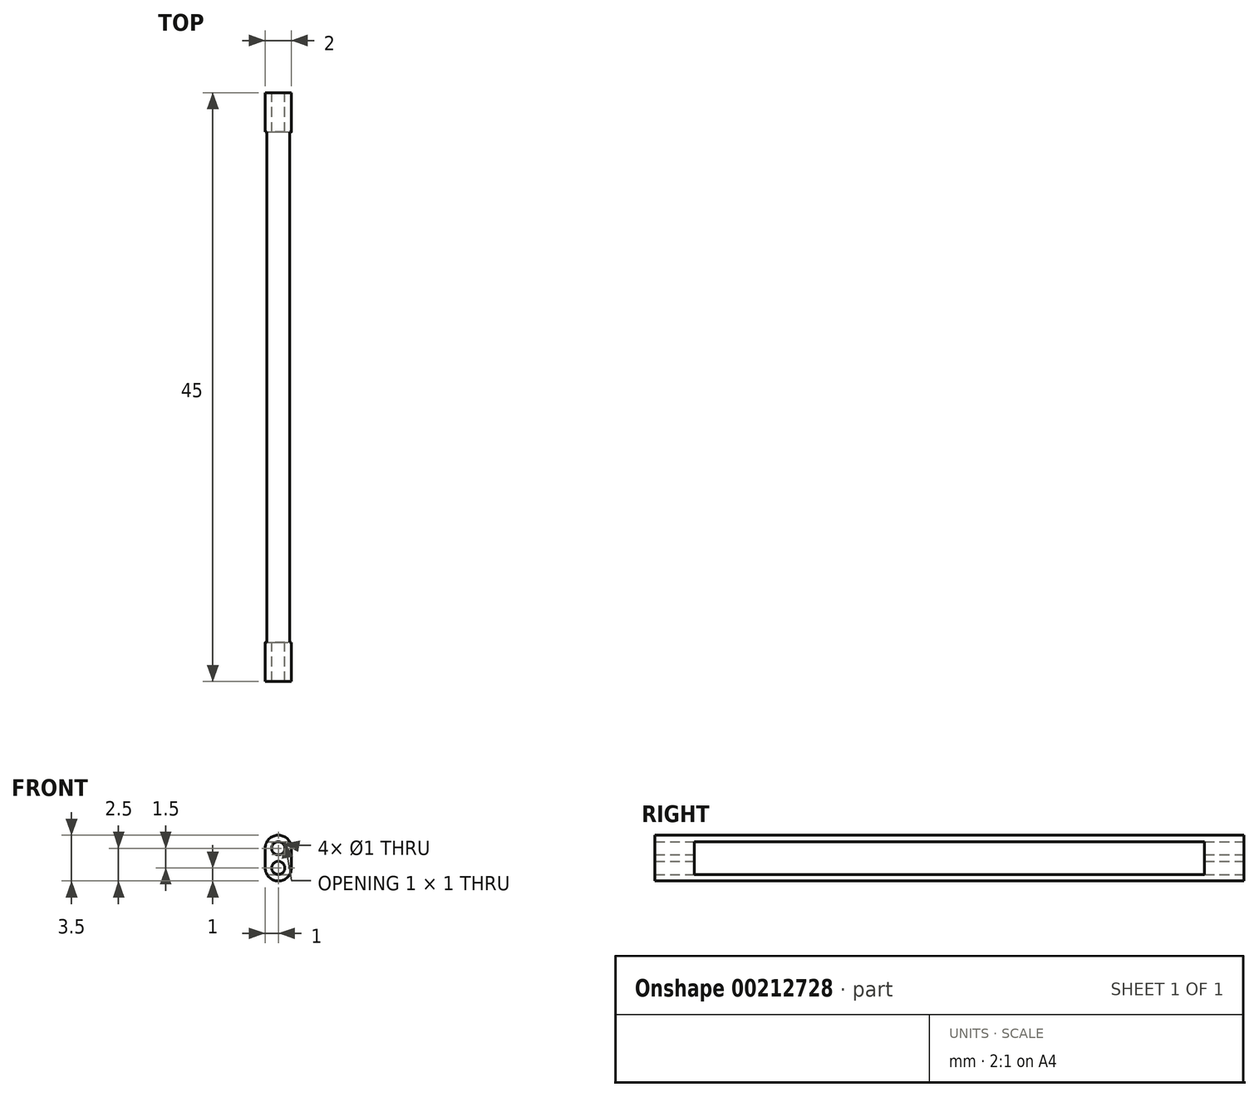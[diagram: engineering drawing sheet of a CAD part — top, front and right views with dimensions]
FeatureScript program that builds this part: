
annotation { "Feature Type Name" : "Feature", "Feature Type Description" : "" }
export const myFeature = defineFeature(function(context is Context, id is Id, definition is map)
    precondition{}
    {
        {
            var Q0;
            Q0=qCreatedBy(makeId("Front.planeOp"),FACE);
            var sketch = newSketch(context, id + "F0", { "sketchPlane" : qUnion([Q0])});
            skLineSegment(sketch, "E0.left", {"start": v(1, -0.75) * mm, "end": v(1, 0.75) * mm});
            skLineSegment(sketch, "E0.right", {"start": v(-1, -0.75) * mm, "end": v(-1, 0.75) * mm});
            skPoint(sketch, "E0.middle", {"position": v(0, 0) * mm});
            skCircle(sketch, "E1", {"center": v(0, 0.75) * mm, "radius": 0.5 * mm});
            skCircle(sketch, "E2.MirrorC", {"center": v(0, -0.75) * mm, "radius": 0.5 * mm});
            skLineSegment(sketch, "E3", {"start": v(-1, 0) * mm, "end": v(1, 0) * mm, "construction": true});
            skArc(sketch, "E4", {"start": v(-1, 0.75) * mm, "mid": v(0, 1.75) * mm, "end": v(1, 0.75) * mm});
            skArc(sketch, "E5", {"start": v(-1, -0.75) * mm, "mid": v(0, -1.75) * mm, "end": v(1, -0.75) * mm});
            skSolve(sketch);
        }
        {
            var Q0;
            Q0 = qSketchRegion(id + "F0", true);
            var Q1;
            Q1=makeQuery(id+"F0.imprint","IMPRINT",FACE,{"disambiguationData":[TD([[makeQuery(id+"F0.imprint","IMPRINT",EDGE,{"derivedFrom":sQuery(id+"F0.wireOp",EDGE,"E0.left")}),1.0]])]});
            extrude(context, id + "F1", {"entities" : qUnion([Q0, Q1]), "depth" : 45 * mm});
        }
        {
            var Q0;
            Q0=makeQuery(id+"F1.opExtrude","SWEPT_FACE",FACE,{"disambiguationData":[OSD([sQuery(id+"F0.wireOp",EDGE,"E0.left")])]});
            var sketch = newSketch(context, id + "F2", { "sketchPlane" : qUnion([Q0])});
            skLineSegment(sketch, "E6.bottom", {"start": v(-3, -1.25) * mm, "end": v(-42, -1.25) * mm});
            skLineSegment(sketch, "E6.top", {"start": v(-3, 1.25) * mm, "end": v(-42, 1.25) * mm});
            skLineSegment(sketch, "E6.left", {"start": v(-3, -1.25) * mm, "end": v(-3, 1.25) * mm});
            skLineSegment(sketch, "E6.right", {"start": v(-42, -1.25) * mm, "end": v(-42, 1.25) * mm});
            skPoint(sketch, "E6.middle", {"position": v(-22.5, 0) * mm});
            skPoint(sketch, "E6.middle.positionSnap0", {"position": v(-22.5, -0.75) * mm});
            skPoint(sketch, "E6.centerSnap0", {"position": v(-22.5, -0.75) * mm});
            skSolve(sketch);
        }
        {
            var Q0;
            Q0 = qSketchRegion(id + "F2", true);
            extrude(context, id + "F3", {"entities" : qUnion([Q0]), "operationType" : NewBodyOperationType.REMOVE, "endBound" : BoundingType.THROUGH_ALL, "oppositeDirection" : true, "depth" : 25 * mm});
        }
    });
